# Revit family: F2AR_2511-2543-2607_OS275
name_source: partatom
category: Finestre
units: mm (PartAtom-declared; Revit-internal decimal feet)

## family parameters
Condiviso = No
Host = Muro
Numero OmniClass = 23.30.20.00
Punto di calcolo locali = Sì
Sempre verticale = Sì
Taglio con vuoti quando caricato = No
Titolo OmniClass = Windows

## types (4) — shared parameters
Altezza di default del davanzale = 800 mm  [stored 2.62467 ft]
Chiusura muro = Per host
Costruzione analitica = <Nessuno>
Descrizione = Finestra anta/ribalta 2 ante
H_Max = 3000 mm  [stored 9.84252 ft]
H_Min = 670 mm
H_man = 500 mm  [stored 1.64042 ft]
H_maniglia = 500 mm  [stored 1.64042 ft]
L_Max = 2000 mm  [stored 6.56168 ft]
L_Min = 1200 mm
Maniglia_alta = 1050 mm  [stored 3.44488 ft]
Maniglia_media = 500 mm  [stored 1.64042 ft]
Modello = OS2 75
Produttore = Secco Sistemi Spa
URL = https://www.seccosistemi.com
n2_scarichi = 2
n3_scarichi = 3
numero_scarichi = 2

## per-type parameters (varying)
| type | Altezza | H | H1 | H_vetro | L | L1 | L_vetro | Larghezza | Larghezza_1A | Larghezza_2A | MATERIALE | Maniglia_bassa | WARNING |
| Acciao Corten | 1500 mm  [stored 4.92126 ft] | 1500 mm  [stored 4.92126 ft] | 1500 mm  [stored 4.92126 ft] | 1424 mm  [stored 4.67192 ft] | 1500 mm  [stored 4.92126 ft] | 1500 mm  [stored 4.92126 ft] | 690 mm  [stored 2.26378 ft] | 1500 mm  [stored 4.92126 ft] | 766 mm  [stored 2.51312 ft] | 766 mm  [stored 2.51312 ft] | Acciaio corten | 750 mm | No |
| Acciaio inox | 1500 mm  [stored 4.92126 ft] | 1500 mm  [stored 4.92126 ft] | 1500 mm  [stored 4.92126 ft] | 1424 mm  [stored 4.67192 ft] | 1200 mm | 1200 mm | 540 mm | 1000 mm  [stored 3.28084 ft] | 616 mm  [stored 2.021 ft] | 616 mm  [stored 2.021 ft] | Acciaio inox, spazzolato | 750 mm | Sì |
| Acciaio zincato | 1500 mm  [stored 4.92126 ft] | 1500 mm  [stored 4.92126 ft] | 1500 mm  [stored 4.92126 ft] | 1424 mm  [stored 4.67192 ft] | 1200 mm | 1200 mm | 540 mm | 1000 mm  [stored 3.28084 ft] | 616 mm  [stored 2.021 ft] | 616 mm  [stored 2.021 ft] | Acciaio | 750 mm | Sì |
| Ottone | 1200 mm | 1200 mm | 1200 mm | 1124 mm  [stored 3.68766 ft] | 1500 mm  [stored 4.92126 ft] | 1500 mm  [stored 4.92126 ft] | 690 mm  [stored 2.26378 ft] | 1500 mm  [stored 4.92126 ft] | 766 mm  [stored 2.51312 ft] | 766 mm  [stored 2.51312 ft] | Ottone | 600 mm | No |

note: [stored X ft] marks values corroborated as IEEE doubles in the binary element streams (Revit-internal decimal feet)
